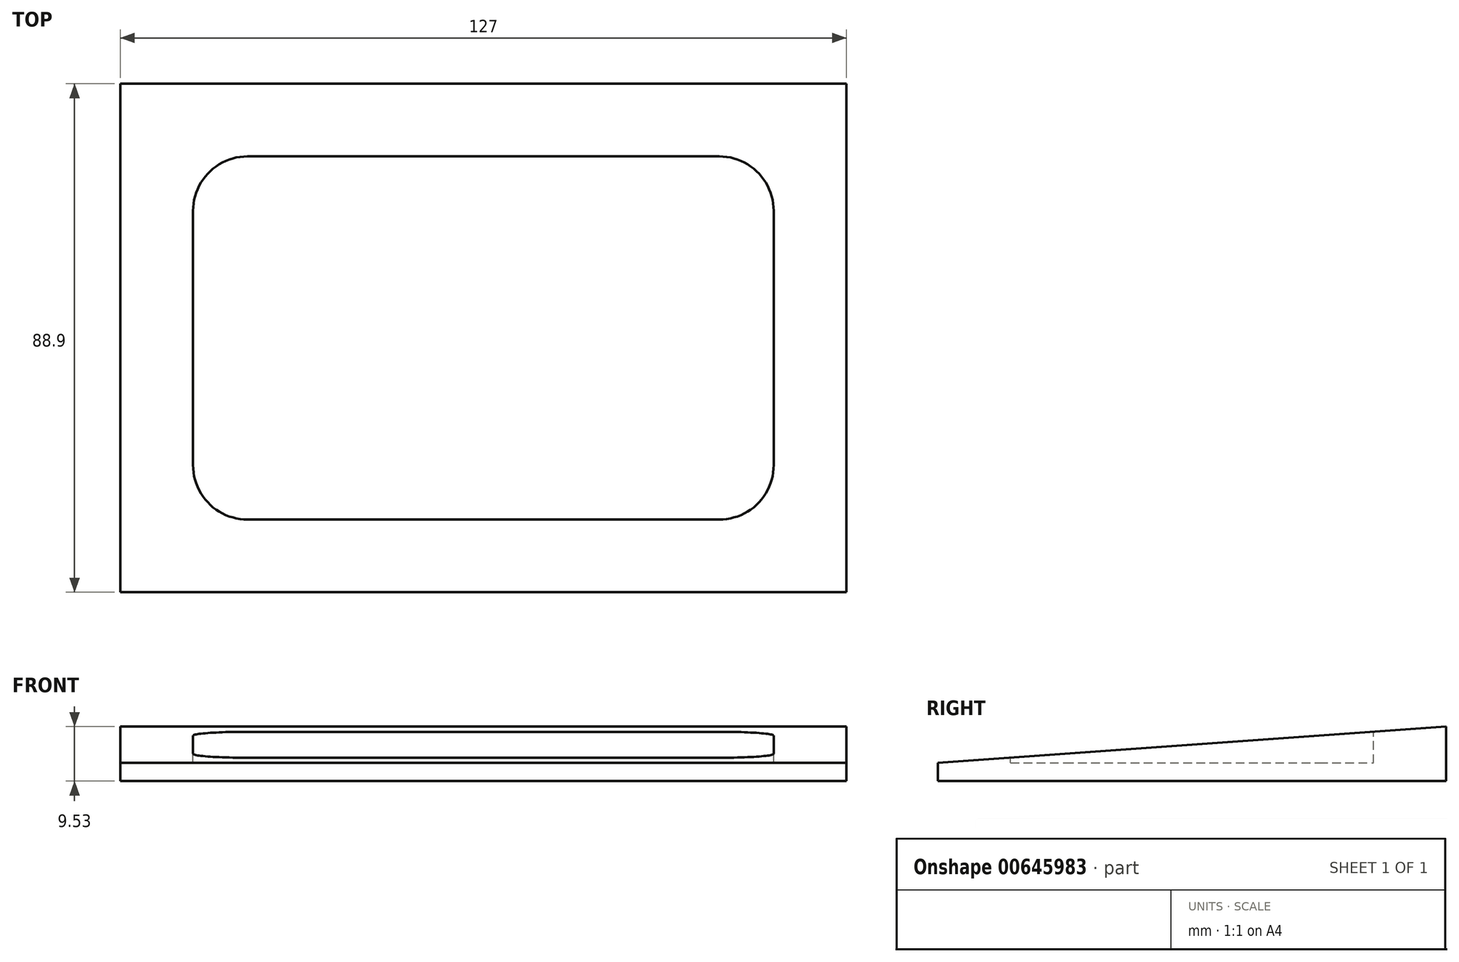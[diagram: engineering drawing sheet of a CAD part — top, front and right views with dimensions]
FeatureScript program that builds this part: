
annotation { "Feature Type Name" : "Feature", "Feature Type Description" : "" }
export const myFeature = defineFeature(function(context is Context, id is Id, definition is map)
    precondition{}
    {
        {
            var Q0;
            Q0=qCreatedBy(makeId("Top.planeOp"),FACE);
            var sketch = newSketch(context, id + "F0", { "sketchPlane" : qUnion([Q0])});
            skLineSegment(sketch, "E0.bottom", {"start": v(0, 0) * mm, "end": v(-127, 0) * mm});
            skLineSegment(sketch, "E0.top", {"start": v(0, -88.9) * mm, "end": v(-127, -88.9) * mm});
            skLineSegment(sketch, "E0.left", {"start": v(0, 0) * mm, "end": v(0, -88.9) * mm});
            skLineSegment(sketch, "E0.right", {"start": v(-127, 0) * mm, "end": v(-127, -88.9) * mm});
            skSolve(sketch);
        }
        {
            var Q0;
            Q0=makeQuery(id+"F0.imprint","IMPRINT",FACE,{"disambiguationData":[TD([[makeQuery(id+"F0.imprint","IMPRINT",EDGE,{"derivedFrom":sQuery(id+"F0.wireOp",EDGE,"E0.bottom")}),1.0]])]});
            extrude(context, id + "F1", {"entities" : qUnion([Q0]), "oppositeDirection" : true, "depth" : 9.52 * mm, "offsetDistance" : 25.4 * mm});
        }
        {
            var Q0;
            Q0=makeQuery(id+"F1.opExtrude","SWEPT_FACE",FACE,{"disambiguationData":[OSD([sQuery(id+"F0.wireOp",EDGE,"E0.right")])]});
            var sketch = newSketch(context, id + "F2", { "sketchPlane" : qUnion([Q0])});
            skLineSegment(sketch, "E1", {"start": v(0, 0) * mm, "end": v(88.9, -6.35) * mm});
            skLineSegment(sketch, "E2", {"start": v(88.9, -6.35) * mm, "end": v(88.9, 0) * mm});
            skLineSegment(sketch, "E3", {"start": v(88.9, 0) * mm, "end": v(0, 0) * mm});
            skSolve(sketch);
        }
        {
            var Q0;
            Q0=makeQuery(id+"F1.opExtrude","CAP_FACE",FACE,{"disambiguationData":[OSD([sQuery(id+"F0.wireOp",EDGE,"E0.bottom"),sQuery(id+"F0.wireOp",EDGE,"E0.top"),sQuery(id+"F0.wireOp",EDGE,"E0.left"),sQuery(id+"F0.wireOp",EDGE,"E0.right")])],"isStart":true});
            var sketch = newSketch(context, id + "F3", { "sketchPlane" : qUnion([Q0])});
            skLineSegment(sketch, "E4.bottom", {"start": v(-114.3, -76.2) * mm, "end": v(-12.7, -76.2) * mm});
            skLineSegment(sketch, "E4.top", {"start": v(-114.3, -12.7) * mm, "end": v(-12.7, -12.7) * mm});
            skLineSegment(sketch, "E4.left", {"start": v(-114.3, -76.2) * mm, "end": v(-114.3, -12.7) * mm});
            skLineSegment(sketch, "E4.right", {"start": v(-12.7, -76.2) * mm, "end": v(-12.7, -12.7) * mm});
            skSolve(sketch);
        }
        {
            var Q0;
            Q0 = qSketchRegion(id + "F3", true);
            extrude(context, id + "F4", {"entities" : qUnion([Q0]), "operationType" : NewBodyOperationType.REMOVE, "oppositeDirection" : true, "depth" : 6.35 * mm, "offsetDistance" : 25.4 * mm});
        }
        {
            var Q0;
            Q0=makeQuery(id+"F4.boolean.opBoolean","COPY",EDGE,{"derivedFrom":makeQuery(id+"F4.opExtrude","SWEPT_EDGE",EDGE,{"disambiguationData":[OSD([sQuery(id+"F3.wireOp",EDGE,"E4.top"),sQuery(id+"F3.wireOp",EDGE,"E4.right")])]})});
            var Q1;
            Q1=makeQuery(id+"F4.boolean.opBoolean","COPY",EDGE,{"derivedFrom":makeQuery(id+"F4.opExtrude","SWEPT_EDGE",EDGE,{"disambiguationData":[OSD([sQuery(id+"F3.wireOp",EDGE,"E4.top"),sQuery(id+"F3.wireOp",EDGE,"E4.left")])]})});
            var Q2;
            Q2=makeQuery(id+"F4.boolean.opBoolean","COPY",EDGE,{"derivedFrom":makeQuery(id+"F4.opExtrude","SWEPT_EDGE",EDGE,{"disambiguationData":[OSD([sQuery(id+"F3.wireOp",EDGE,"E4.bottom"),sQuery(id+"F3.wireOp",EDGE,"E4.left")])]})});
            var Q3;
            Q3=makeQuery(id+"F4.boolean.opBoolean","COPY",EDGE,{"derivedFrom":makeQuery(id+"F4.opExtrude","SWEPT_EDGE",EDGE,{"disambiguationData":[OSD([sQuery(id+"F3.wireOp",EDGE,"E4.bottom"),sQuery(id+"F3.wireOp",EDGE,"E4.right")])]})});
            fillet(context, id + "F5", {"entities" : qUnion([Q0, Q1, Q2, Q3]), "radius" : 9.52 * mm, "tangentPropagation" : true, "allowEdgeOverflow" : false});
        }
        {
            var Q0;
            Q0=makeQuery(id+"F2.imprint","IMPRINT",FACE,{"disambiguationData":[TD([[makeQuery(id+"F2.imprint","IMPRINT",EDGE,{"derivedFrom":sQuery(id+"F2.wireOp",EDGE,"E1")}),1.0]])]});
            extrude(context, id + "F6", {"entities" : qUnion([Q0]), "operationType" : NewBodyOperationType.REMOVE, "endBound" : BoundingType.THROUGH_ALL, "oppositeDirection" : true, "depth" : 25.4 * mm, "offsetDistance" : 25.4 * mm});
        }
    });
